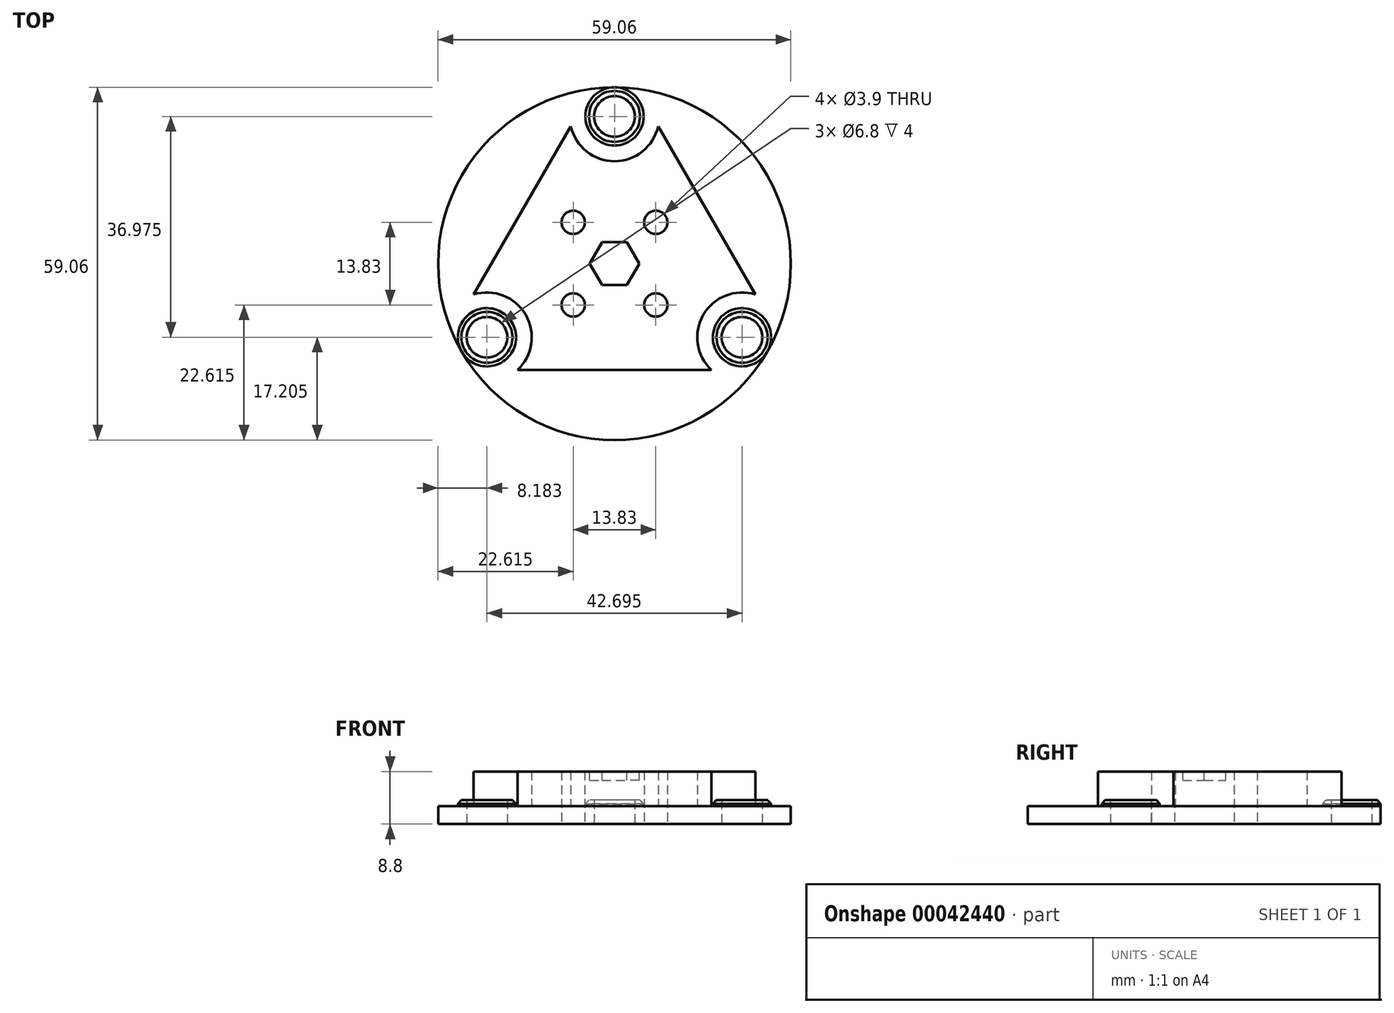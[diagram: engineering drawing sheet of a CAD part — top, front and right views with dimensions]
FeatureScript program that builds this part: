
annotation { "Feature Type Name" : "Feature", "Feature Type Description" : "" }
export const myFeature = defineFeature(function(context is Context, id is Id, definition is map)
    precondition{}
    {
        {
            var Q0;
            Q0=qCreatedBy(makeId("Top.planeOp"),FACE);
            var sketch = newSketch(context, id + "F0", { "sketchPlane" : qUnion([Q0])});
            skCircle(sketch, "E0", {"center": v(0, 0) * mm, "radius": 30 * mm, "construction": true});
            skCircle(sketch, "E1", {"center": v(0, 0) * mm, "radius": 31 * mm, "construction": true});
            skLineSegment(sketch, "E2", {"start": v(0, 30) * mm, "end": v(0, 31) * mm, "construction": true});
            skLineSegment(sketch, "E3", {"start": v(0, 30) * mm, "end": v(0, 0) * mm, "construction": true});
            skCircle(sketch, "E4", {"center": v(0, 24.65) * mm, "radius": 6.35 * mm, "construction": true});
            skCircle(sketch, "E5", {"center": v(0, 24.65) * mm, "radius": 3.4 * mm});
            skCircle(sketch, "E6.1.0", {"center": v(-21.35, -12.32) * mm, "radius": 3.4 * mm});
            skCircle(sketch, "E6.2.0", {"center": v(21.35, -12.33) * mm, "radius": 3.4 * mm});
            skLineSegment(sketch, "E7", {"start": v(-24.3, -14.02) * mm, "end": v(-26.85, -15.5) * mm, "construction": true});
            skPoint(sketch, "E8", {"position": v(-25.57, -14.76) * mm});
            skCircle(sketch, "E9", {"center": v(0, 0) * mm, "radius": 29.52 * mm});
            skSolve(sketch);
        }
        {
            var Q0;
            Q0=qSketchRegion(id+"F0",true);
            extrude(context, id + "F1", {"entities" : qUnion([Q0]), "depth" : 3 * mm});
        }
        {
            var Q0;
            Q0=makeQuery(id+"F1.opExtrude","CAP_FACE",FACE,{"disambiguationData":[OSD([sQuery(id+"F0.wireOp",EDGE,"E5"),sQuery(id+"F0.wireOp",EDGE,"E6.1.0"),sQuery(id+"F0.wireOp",EDGE,"E6.2.0"),sQuery(id+"F0.wireOp",EDGE,"E9")])],"isStart":false});
            var sketch = newSketch(context, id + "F2", { "sketchPlane" : qUnion([Q0])});
            skCircle(sketch, "E10", {"center": v(0, 24.65) * mm, "radius": 4.88 * mm});
            skCircle(sketch, "E11", {"center": v(21.35, -12.33) * mm, "radius": 4.88 * mm});
            skCircle(sketch, "E12", {"center": v(-21.35, -12.32) * mm, "radius": 4.87 * mm});
            skCircle(sketch, "E13.0", {"center": v(0, 24.65) * mm, "radius": 3.4 * mm});
            skCircle(sketch, "E13.1", {"center": v(-21.35, -12.32) * mm, "radius": 3.4 * mm});
            skCircle(sketch, "E13.2", {"center": v(21.35, -12.33) * mm, "radius": 3.4 * mm});
            skSolve(sketch);
        }
        {
            var Q0;
            Q0=qSketchRegion(id+"F2",true);
            extrude(context, id + "F3", {"entities" : qUnion([Q0]), "operationType" : NewBodyOperationType.ADD, "depth" : 1 * mm});
        }
        {
            var Q0;
            Q0=makeQuery(id+"F3.opExtrude","CAP_EDGE",EDGE,{"disambiguationData":[OSD([sQuery(id+"F2.wireOp",EDGE,"E12")])],"isStart":false});
            var Q1;
            Q1=makeQuery(id+"F3.opExtrude","CAP_EDGE",EDGE,{"disambiguationData":[OSD([sQuery(id+"F2.wireOp",EDGE,"E11")])],"isStart":false});
            var Q2;
            Q2=makeQuery(id+"F3.opExtrude","CAP_EDGE",EDGE,{"disambiguationData":[OSD([sQuery(id+"F2.wireOp",EDGE,"E10")])],"isStart":false});
            chamfer(context, id + "F4", {"entities" : qUnion([Q0, Q1, Q2]), "width" : 0.6 * mm, "tangentPropagation" : true});
        }
        {
            var Q0;
            Q0=makeQuery(id+"F1.opExtrude","CAP_FACE",FACE,{"disambiguationData":[OSD([sQuery(id+"F0.wireOp",EDGE,"E5"),sQuery(id+"F0.wireOp",EDGE,"E6.1.0"),sQuery(id+"F0.wireOp",EDGE,"E6.2.0"),sQuery(id+"F0.wireOp",EDGE,"E9")])],"isStart":false});
            var sketch = newSketch(context, id + "F5", { "sketchPlane" : qUnion([Q0])});
            skCircle(sketch, "E14", {"center": v(0, 24.65) * mm, "radius": 7.5 * mm, "construction": true});
            skCircle(sketch, "E15", {"center": v(-21.35, -12.32) * mm, "radius": 7.5 * mm, "construction": true});
            skCircle(sketch, "E16", {"center": v(21.35, -12.33) * mm, "radius": 7.5 * mm, "construction": true});
            skLineSegment(sketch, "E17", {"start": v(-6.5, 28.4) * mm, "end": v(-27.84, -8.58) * mm, "construction": true});
            skLineSegment(sketch, "E18", {"start": v(6.5, 28.4) * mm, "end": v(27.84, -8.58) * mm, "construction": true});
            skLineSegment(sketch, "E19", {"start": v(-21.35, -19.82) * mm, "end": v(21.35, -19.82) * mm, "construction": true});
            skLineSegment(sketch, "E20", {"start": v(-7.31, 22.98) * mm, "end": v(-23.56, -5.16) * mm});
            skLineSegment(sketch, "E21", {"start": v(7.31, 22.98) * mm, "end": v(23.56, -5.16) * mm});
            skLineSegment(sketch, "E22", {"start": v(16.25, -17.82) * mm, "end": v(-16.25, -17.82) * mm});
            skLineSegment(sketch, "E23", {"start": v(0, -17.82) * mm, "end": v(0, -19.82) * mm, "construction": true});
            skLineSegment(sketch, "E24", {"start": v(-15.44, 8.91) * mm, "end": v(-17.17, 9.91) * mm, "construction": true});
            skLineSegment(sketch, "E25", {"start": v(15.44, 8.91) * mm, "end": v(17.17, 9.91) * mm, "construction": true});
            skArc(sketch, "E26", {"start": v(-7.31, 22.98) * mm, "mid": v(0, 17.15) * mm, "end": v(7.31, 22.98) * mm});
            skArc(sketch, "E27", {"start": v(23.56, -5.16) * mm, "mid": v(14.85, -8.57) * mm, "end": v(16.25, -17.82) * mm});
            skArc(sketch, "E28", {"start": v(-16.25, -17.82) * mm, "mid": v(-14.85, -8.57) * mm, "end": v(-23.56, -5.16) * mm});
            skSolve(sketch);
        }
        {
            var Q0;
            Q0=qSketchRegion(id+"F5",true);
            extrude(context, id + "F6", {"entities" : qUnion([Q0]), "operationType" : NewBodyOperationType.ADD, "depth" : 5.8 * mm});
        }
        {
            var Q0;
            Q0=makeQuery(id+"F1.opExtrude","CAP_FACE",FACE,{"disambiguationData":[OSD([sQuery(id+"F0.wireOp",EDGE,"E5"),sQuery(id+"F0.wireOp",EDGE,"E6.1.0"),sQuery(id+"F0.wireOp",EDGE,"E6.2.0"),sQuery(id+"F0.wireOp",EDGE,"E9")])],"isStart":true});
            var sketch = newSketch(context, id + "F7", { "sketchPlane" : qUnion([Q0])});
            skLineSegment(sketch, "E29", {"start": v(0, 0) * mm, "end": v(0, -24.65) * mm, "construction": true});
            skCircle(sketch, "E30.cCircle", {"center": v(0, 0) * mm, "radius": 9.78 * mm, "construction": true});
            skLineSegment(sketch, "E30.0", {"start": v(6.91, -6.91) * mm, "end": v(-6.91, -6.91) * mm, "construction": true});
            skLineSegment(sketch, "E30.1", {"start": v(-6.91, -6.91) * mm, "end": v(-6.91, 6.91) * mm, "construction": true});
            skLineSegment(sketch, "E30.2", {"start": v(-6.91, 6.91) * mm, "end": v(6.91, 6.91) * mm, "construction": true});
            skLineSegment(sketch, "E30.3", {"start": v(6.91, 6.91) * mm, "end": v(6.91, -6.91) * mm, "construction": true});
            skCircle(sketch, "E31", {"center": v(6.91, 6.91) * mm, "radius": 1.95 * mm});
            skCircle(sketch, "E32.1.0", {"center": v(-6.91, 6.91) * mm, "radius": 1.95 * mm});
            skCircle(sketch, "E32.2.0", {"center": v(-6.91, -6.91) * mm, "radius": 1.95 * mm});
            skCircle(sketch, "E32.3.0", {"center": v(6.91, -6.91) * mm, "radius": 1.95 * mm});
            skSolve(sketch);
        }
        {
            var Q0;
            Q0=qSketchRegion(id+"F7",true);
            extrude(context, id + "F8", {"entities" : qUnion([Q0]), "operationType" : NewBodyOperationType.REMOVE, "endBound" : BoundingType.THROUGH_ALL, "oppositeDirection" : true, "depth" : 25 * mm});
        }
        {
            var Q0;
            Q0=makeQuery(id+"F6.opExtrude","CAP_FACE",FACE,{"disambiguationData":[OSD([sQuery(id+"F5.wireOp",EDGE,"E20"),sQuery(id+"F5.wireOp",EDGE,"E21"),sQuery(id+"F5.wireOp",EDGE,"E22"),sQuery(id+"F5.wireOp",EDGE,"b30b8c31-8519-46e4-bd01-4f495bb6e8cf"),sQuery(id+"F5.wireOp",EDGE,"E26"),sQuery(id+"F5.wireOp",EDGE,"E27")])],"isStart":false});
            var sketch = newSketch(context, id + "F9", { "sketchPlane" : qUnion([Q0])});
            skCircle(sketch, "E33.cCircle", {"center": v(0, 0) * mm, "radius": 3.6 * mm, "construction": true});
            skLineSegment(sketch, "E33.0", {"start": v(-2.08, 3.6) * mm, "end": v(2.08, 3.6) * mm});
            skLineSegment(sketch, "E33.1", {"start": v(2.08, 3.6) * mm, "end": v(4.16, 0) * mm});
            skLineSegment(sketch, "E33.2", {"start": v(4.16, 0) * mm, "end": v(2.08, -3.6) * mm});
            skLineSegment(sketch, "E33.3", {"start": v(2.08, -3.6) * mm, "end": v(-2.08, -3.6) * mm});
            skLineSegment(sketch, "E33.4", {"start": v(-2.08, -3.6) * mm, "end": v(-4.16, 0) * mm});
            skLineSegment(sketch, "E33.5", {"start": v(-4.16, 0) * mm, "end": v(-2.08, 3.6) * mm});
            skPoint(sketch, "E33.0.midPoint", {"position": v(0, 3.6) * mm});
            skSolve(sketch);
        }
        {
            var Q0;
            Q0=qSketchRegion(id+"F9",true);
            extrude(context, id + "F10", {"entities" : qUnion([Q0]), "operationType" : NewBodyOperationType.REMOVE, "oppositeDirection" : true, "depth" : 1.45 * mm});
        }
    });
